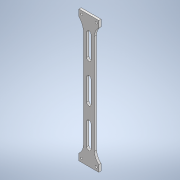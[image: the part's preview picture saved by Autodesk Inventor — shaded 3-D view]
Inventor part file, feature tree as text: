
AUTODESK INVENTOR PART (.ipt)
format: ipt  version: 2020 (Build 240168000, 168)  size: 171,008 bytes
history: native  units: mm
features: other x5, reference x3, extrude x2, sketch x2, projected_geometry x1
ambient origin geometry x8: Origin, YZ Plane, XZ Plane, XY Plane, X Axis, Y Axis, Z Axis, Center Point
bodies: Solid1 (feature_tree)
feature tree (13):
  extrude  "Extrusion1"  Depth=28.5mm
  extrude  "Extrusion2"  Depth=2.0mm
  sketch  "Sketch1"  dims[d0=170.0mm d1=28.5mm]
  reference  "Reference1"
  reference  "Reference2"
  reference  "Reference3"
  sketch  "Sketch2"  dims[d2=113.0mm d3=113.0mm d4=2.0mm d5=2.0mm d6=18.0mm d7=6.0mm d8=18.0mm d9=6.0mm d10=10.0mm d11=90.0mm d12=2.0mm d13=0.0mm d14=10.0mm d15=4.0mm d16=35.0mm d17=10.0mm d18=4.0mm d19=35.0mm d20=10.0mm d21=4.0mm d22=2.0mm d23=0.0mm]
  projected_geometry  "Projected Loop1"
  parser-record x1  (decoder bookkeeping rows leaked as tree rows — omitted from the tree; the rows remain in map.json)
  other  "delta_1.iam"
  other  "eye_bearing:1"
  other  "bbearing_holder_1:1"
  other  "arm_3:1"
note: 1 file-system path scrubbed to <path> (originals preserved in map.json)
